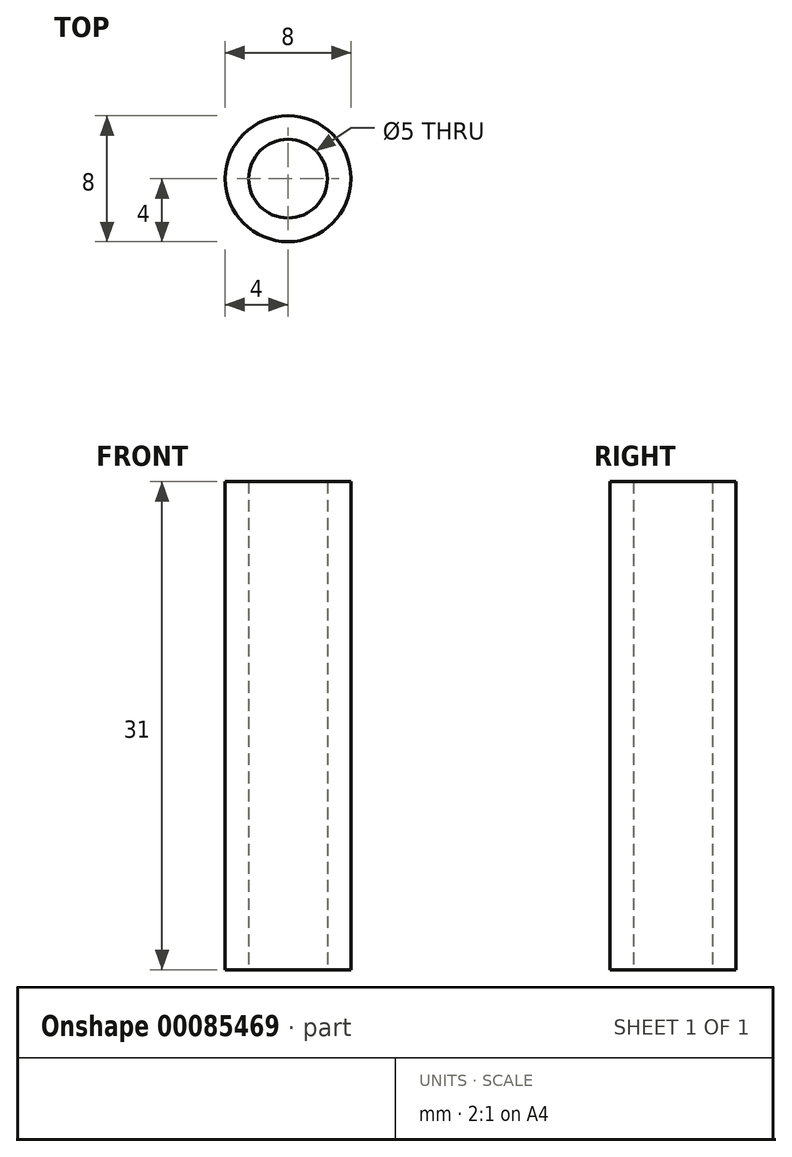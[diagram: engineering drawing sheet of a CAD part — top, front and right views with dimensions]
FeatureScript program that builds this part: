
annotation { "Feature Type Name" : "Feature", "Feature Type Description" : "" }
export const myFeature = defineFeature(function(context is Context, id is Id, definition is map)
    precondition{}
    {
        {
            var Q0;
            Q0=qCreatedBy(makeId("Top.planeOp"),FACE);
            var sketch = newSketch(context, id + "F0", { "sketchPlane" : qUnion([Q0])});
            skCircle(sketch, "E0", {"center": v(0, 0) * mm, "radius": 2.5 * mm});
            skCircle(sketch, "E1", {"center": v(0, 0) * mm, "radius": 4 * mm});
            skSolve(sketch);
        }
        {
            var Q0;
            Q0=makeQuery(id+"F0.imprint","IMPRINT",FACE,{"disambiguationData":[TD([[makeQuery(id+"F0.imprint","IMPRINT",EDGE,{"derivedFrom":sQuery(id+"F0.wireOp",EDGE,"E0")}),-1.0]])]});
            extrude(context, id + "F1", {"entities" : qUnion([Q0]), "depth" : 31 * mm});
        }
    });
